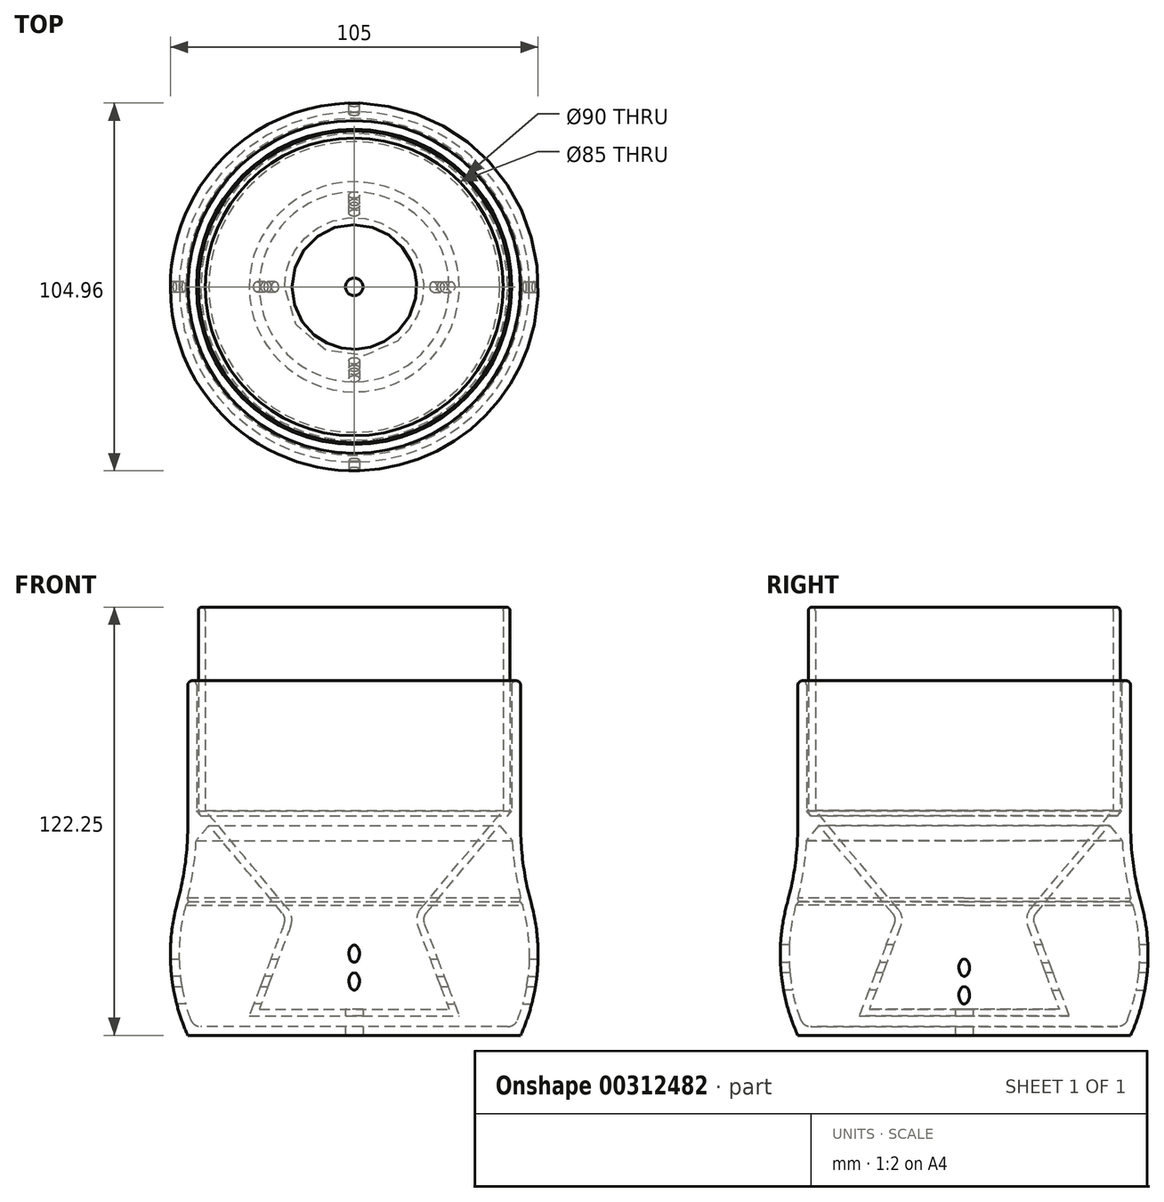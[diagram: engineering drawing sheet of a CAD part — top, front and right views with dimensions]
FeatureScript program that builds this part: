
annotation { "Feature Type Name" : "Feature", "Feature Type Description" : "" }
export const myFeature = defineFeature(function(context is Context, id is Id, definition is map)
    precondition{}
    {
        {
            var Q0;
            Q0=qCreatedBy(makeId("Front.planeOp"),FACE);
            var sketch = newSketch(context, id + "F0", { "sketchPlane" : qUnion([Q0])});
            skLineSegment(sketch, "E0", {"start": v(-47.5, 100) * mm, "end": v(-47.5, 60) * mm});
            skArc(sketch, "E1", {"start": v(-47.5, 60) * mm, "mid": v(-48.25, 48.81) * mm, "end": v(-50.5, 37.83) * mm});
            skArc(sketch, "E2", {"start": v(-50.5, 37.83) * mm, "mid": v(-52.33, 18.65) * mm, "end": v(-47.5, 0) * mm});
            skLineSegment(sketch, "E3", {"start": v(-47.5, 0) * mm, "end": v(0, 0) * mm});
            skLineSegment(sketch, "E4", {"start": v(0, 0) * mm, "end": v(0, 134.65) * mm, "construction": true});
            skLineSegment(sketch, "E5.0", {"start": v(-45.86, 2.5) * mm, "end": v(0, 2.5) * mm});
            skArc(sketch, "E5.1", {"start": v(-48.09, 37.16) * mm, "mid": v(-49.9, 19.65) * mm, "end": v(-45.86, 2.5) * mm});
            skArc(sketch, "E5.2", {"start": v(-45, 60) * mm, "mid": v(-45.78, 48.48) * mm, "end": v(-48.09, 37.16) * mm});
            skLineSegment(sketch, "E5.3", {"start": v(-45, 100) * mm, "end": v(-45, 60) * mm});
            skLineSegment(sketch, "E6", {"start": v(0, 2.5) * mm, "end": v(0, 0) * mm});
            skArc(sketch, "E7", {"start": v(-47.5, 100) * mm, "mid": v(-46.25, 101.25) * mm, "end": v(-45, 100) * mm});
            skSolve(sketch);
        }
        {
            var Q0;
            Q0 = qSketchRegion(id + "F0", true);
            var Q1;
            Q1=sQuery(id+"F0.wireOp",EDGE,"E4");
            revolve(context, id + "F1", {"entities" : qUnion([Q0]), "axis" : qUnion([Q1]), "revolveType" : RevolveType.FULL});
        }
        {
            var Q0;
            Q0=qCreatedBy(makeId("Front.planeOp"),FACE);
            var sketch = newSketch(context, id + "F2", { "sketchPlane" : qUnion([Q0])});
            skLineSegment(sketch, "E8", {"start": v(-44.5, 121.25) * mm, "end": v(-44.5, 64.59) * mm});
            skLineSegment(sketch, "E9", {"start": v(-43.8, 62.66) * mm, "end": v(-20.5, 34.9) * mm});
            skLineSegment(sketch, "E10", {"start": v(-20, 31.91) * mm, "end": v(-30, 5.5) * mm});
            skLineSegment(sketch, "E11", {"start": v(-30, 5.5) * mm, "end": v(0, 5.5) * mm});
            skPoint(sketch, "E12.visualSharp", {"position": v(-44.5, 63.5) * mm});
            skArc(sketch, "E12.filletArc", {"start": v(-44.5, 64.59) * mm, "mid": v(-44.32, 63.56) * mm, "end": v(-43.8, 62.66) * mm});
            skPoint(sketch, "E13.visualSharp", {"position": v(-19.38, 33.56) * mm});
            skArc(sketch, "E13.filletArc", {"start": v(-20, 31.91) * mm, "mid": v(-19.85, 33.48) * mm, "end": v(-20.5, 34.9) * mm});
            skLineSegment(sketch, "E14.0", {"start": v(-27.1, 7.5) * mm, "end": v(0, 7.5) * mm});
            skLineSegment(sketch, "E14.1", {"start": v(-42.5, 121.25) * mm, "end": v(-42.5, 64.22) * mm});
            skLineSegment(sketch, "E14.2", {"start": v(-42.5, 64.22) * mm, "end": v(-18.98, 36.19) * mm});
            skArc(sketch, "E14.3", {"start": v(-18.13, 31.2) * mm, "mid": v(-17.88, 33.81) * mm, "end": v(-18.98, 36.19) * mm});
            skLineSegment(sketch, "E14.4", {"start": v(-18.13, 31.2) * mm, "end": v(-27.1, 7.5) * mm});
            skArc(sketch, "E15", {"start": v(-44.5, 121.25) * mm, "mid": v(-43.5, 122.25) * mm, "end": v(-42.5, 121.25) * mm});
            skLineSegment(sketch, "E16", {"start": v(0, 5.5) * mm, "end": v(0, 7.5) * mm});
            skSolve(sketch);
        }
        {
            var Q0;
            Q0 = qSketchRegion(id + "F2", true);
            var Q1;
            Q1=sQuery(id+"F0.wireOp",EDGE,"E4");
            revolve(context, id + "F3", {"entities" : qUnion([Q0]), "axis" : qUnion([Q1]), "revolveType" : RevolveType.FULL});
        }
        {
            var Q0;
            Q0=qCreatedBy(makeId("Front.planeOp"),FACE);
            var sketch = newSketch(context, id + "F4", { "sketchPlane" : qUnion([Q0])});
            skLineSegment(sketch, "E17", {"start": v(-45, 64.1) * mm, "end": v(-45, 55.75) * mm});
            skLineSegment(sketch, "E18", {"start": v(-45, 55.75) * mm, "end": v(-41.5, 59.92) * mm});
            skLineSegment(sketch, "E19", {"start": v(-41.5, 59.92) * mm, "end": v(-45, 64.1) * mm});
            skArc(sketch, "E20.0", {"start": v(-47.56, 39.16) * mm, "mid": v(-47.82, 38.16) * mm, "end": v(-48.09, 37.16) * mm});
            skLineSegment(sketch, "E21", {"start": v(-48.09, 37.16) * mm, "end": v(-47.25, 38.16) * mm});
            skLineSegment(sketch, "E22", {"start": v(-47.25, 38.16) * mm, "end": v(-47.56, 39.16) * mm});
            skPoint(sketch, "E23.orphan", {"position": v(-45, 60) * mm});
            skLineSegment(sketch, "E24", {"start": v(-45, 55.75) * mm, "end": v(-46.4, 54.07) * mm});
            skLineSegment(sketch, "E25", {"start": v(-46.4, 54.07) * mm, "end": v(-45, 60) * mm});
            skSolve(sketch);
        }
        {
            var Q0;
            Q0 = qSketchRegion(id + "F4", true);
            var Q1;
            Q1=sQuery(id+"F0.wireOp",EDGE,"E4");
            revolve(context, id + "F5", {"operationType" : NewBodyOperationType.ADD, "entities" : qUnion([Q0]), "axis" : qUnion([Q1]), "revolveType" : RevolveType.FULL});
        }
        {
            var Q0;
            Q0=qCreatedBy(makeId("Front.planeOp"),FACE);
            var sketch = newSketch(context, id + "F6", { "sketchPlane" : qUnion([Q0])});
            skLineSegment(sketch, "E26", {"start": v(0, 7.5) * mm, "end": v(0, 15.4) * mm, "construction": true});
            skLineSegment(sketch, "E27", {"start": v(0, 15.4) * mm, "end": v(0, 23.3) * mm, "construction": true});
            skLineSegment(sketch, "E28", {"start": v(0, 23.3) * mm, "end": v(0, 31.2) * mm, "construction": true});
            skEllipse(sketch, "E29", {"center": v(0, 23.3) * mm, "majorRadius": 2.5 * mm, "minorRadius": 1.5 * mm, "majorAxis": v(0, 1)});
            skEllipse(sketch, "E30", {"center": v(0, 15.4) * mm, "majorRadius": 2.5 * mm, "minorRadius": 1.5 * mm, "majorAxis": v(0, 1)});
            skSolve(sketch);
        }
        {
            var Q0;
            Q0 = qSketchRegion(id + "F6", true);
            extrude(context, id + "F7", {"entities" : qUnion([Q0]), "operationType" : NewBodyOperationType.REMOVE, "endBound" : BoundingType.THROUGH_ALL, "oppositeDirection" : true, "depth" : 25 * mm, "hasSecondDirection" : true, "secondDirectionBound" : BoundingType.THROUGH_ALL, "secondDirectionOppositeDirection" : false, "secondDirectionDepth" : 25 * mm});
        }
        {
            var Q0;
            Q0=qCreatedBy(makeId("Right.planeOp"),FACE);
            var sketch = newSketch(context, id + "F8", { "sketchPlane" : qUnion([Q0])});
            skEllipse(sketch, "E31", {"center": v(0, 19.35) * mm, "majorRadius": 2.5 * mm, "minorRadius": 1.5 * mm, "majorAxis": v(0, 1)});
            skEllipse(sketch, "E32", {"center": v(0, 11.45) * mm, "majorRadius": 2.5 * mm, "minorRadius": 1.5 * mm, "majorAxis": v(0, 1)});
            skSolve(sketch);
        }
        {
            var Q0;
            Q0 = qSketchRegion(id + "F8", true);
            extrude(context, id + "F9", {"entities" : qUnion([Q0]), "operationType" : NewBodyOperationType.REMOVE, "endBound" : BoundingType.THROUGH_ALL, "oppositeDirection" : true, "depth" : 25 * mm, "hasSecondDirection" : true, "secondDirectionBound" : BoundingType.THROUGH_ALL, "secondDirectionOppositeDirection" : false, "secondDirectionDepth" : 25 * mm});
        }
        {
            var Q0;
            Q0=makeQuery(id+"F1.opRevolve","SWEPT_EDGE",EDGE,{"disambiguationData":[OSD([sQuery(id+"F0.wireOp",EDGE,"E5.0"),sQuery(id+"F0.wireOp",EDGE,"E5.1")])]});
            fillet(context, id + "F10", {"entities" : qUnion([Q0]), "radius" : 3 * mm, "tangentPropagation" : true, "allowEdgeOverflow" : false});
        }
        {
            var Q0;
            Q0=qCreatedBy(makeId("Top.planeOp"),FACE);
            var sketch = newSketch(context, id + "F11", { "sketchPlane" : qUnion([Q0])});
            skCircle(sketch, "E33", {"center": v(0, 0) * mm, "radius": 2.5 * mm});
            skSolve(sketch);
        }
        {
            var Q0;
            Q0 = qSketchRegion(id + "F11", true);
            extrude(context, id + "F12", {"entities" : qUnion([Q0]), "operationType" : NewBodyOperationType.REMOVE, "endBound" : BoundingType.THROUGH_ALL, "depth" : 25 * mm});
        }
    });
